# Revit family: Class-I-Fan_VBBB-CW-BHD_Carnes
name_source: partatom
category: Mechanical Equipment
revit_build: Autodesk Revit Architecture 2012 (Build: 20110309_2315(x64)
units: mm (PartAtom-declared; Revit-internal decimal feet)

## types (12) — shared parameters
04 CSI = 23 34 23
95 CSI = 15830
Angle = 270.00°
Assembly Code = D3040200
Catalog URL = http://www.carnes.com
Description = Cetrifugal Blowers
Housing = Aluminum-Carnes-Spun-Brushed
Housing Rotation CW DBD = Yes
IOM Instructions URL = http://www.carnes.com
Manufacturer = Carnes Company
Manufacturer Fax = 608-845-6470
Motor Cover = No
Product Page URL = http://www.carnes.com
URL = http://www.carnes.com
Warranty URL = http://www.carnes.com
Weather Cover = Yes
ecoScorecard Product Page = http://ecoscorecard.com
zero-valued in all types: Default Elevation

## per-type parameters (varying)
- VBBB-CW-BHD 12: 01=14.88 "; A=13 "; B=9.75 "; C=13.25 "; D=14.5 "; DX=1 "; Drip=4.88 "; Drip1=4.88 "; G=16 "; H=24.5 "; HA=9.75 "; HC=13.94 "; HE=10.56 "; HG=9.31 "; HJ=9.25 "; HN=12.94 "; J=7.44 "; KL=2 "; Model=VBBB 12; Motor Pedastal Stand=11.88 "; P=19.75 "; Radius=6.63 "; SD=1 "; SD Radius=0.5 "; SE=2.75 "; Support Plate Drip=17.63 "; Weather Cover Height=22.38 "; Weather Cover Length=17.38 "; Weather Cover Width=16 "
- VBBB-CW-BHD 13: 01=14.91 "; A=14.31 "; B=10.81 "; C=14.56 "; D=15.75 "; DX=1 "; Drip=7.4 "; Drip1=5.41 "; G=17.5 "; H=25.63 "; HA=10.75 "; HC=15.25 "; HE=11.63 "; HG=10.25 "; HJ=10.25 "; HN=14.25 "; J=8 "; KL=2 "; Model=VBBB 13; Motor Pedastal Stand=11.91 "; P=20.31 "; Radius=7.28 "; SD=1 "; SD Radius=0.5 "; SE=2.75 "; Support Plate Drip=15.75 "; Weather Cover Height=22.8 "; Weather Cover Length=17.38 "; Weather Cover Width=17.5 "
- VBBB-CW-BHD 15: 01=17.16 "; A=15.88 "; B=11.94 "; C=16.19 "; D=17.75 "; DX=1 "; Drip=6.9 "; Drip1=5.97 "; G=19 "; H=28.75 "; HA=11.94 "; HC=16.81 "; HE=12.88 "; HG=11.38 "; HJ=11.44 "; HN=15.81 "; J=9.06 "; KL=2.5 "; Model=VBBB 15; Motor Pedastal Stand=13.66 "; P=23.13 "; Radius=8.1 "; SD=1 "; SD Radius=0.5 "; SE=3.25 "; Support Plate Drip=17.75 "; Weather Cover Height=25.5 "; Weather Cover Length=19.88 "; Weather Cover Width=19 "
- VBBB-CW-BHD 16: 01=17.16 "; A=17.44 "; B=13.19 "; C=17.75 "; D=19 "; DX=1 "; Drip=6.9 "; Drip1=6.6 "; G=20.5 "; H=30.13 "; HA=13.13 "; HC=18.38 "; HE=14.13 "; HG=12.5 "; HJ=12.63 "; HN=17.38 "; J=9.69 "; KL=2.5 "; Model=VBBB 16; Motor Pedastal Stand=13.66 "; P=23.75 "; Radius=8.88 "; SD=1 "; SD Radius=0.5 "; SE=3.25 "; Support Plate Drip=19 "; Weather Cover Height=28 "; Weather Cover Length=19.88 "; Weather Cover Width=20.5 "
- VBBB-CW-BHD 18: 01=20.66 "; A=19.38 "; B=14.56 "; C=19.5 "; D=21 "; DX=1.25 "; Drip=6.4 "; Drip1=7.28 "; G=22.5 "; H=34.38 "; HA=14.5 "; HC=20.56 "; HE=15.69 "; HG=13.81 "; HJ=14 "; HN=19.31 "; J=10.88 "; KL=3 "; Model=VBBB 18; Motor Pedastal Stand=16.66 "; P=27.94 "; Radius=9.75 "; SD=1.19 "; SD Radius=0.6 "; SE=3.75 "; Support Plate Drip=21 "; Weather Cover Height=32 "; Weather Cover Length=23.25 "; Weather Cover Width=22.5 "
- VBBB-CW-BHD 20: 01=20.66 "; A=21.19 "; B=15.94 "; C=21.38 "; D=22.75 "; DX=1.25 "; Drip=6.4 "; Drip1=7.97 "; G=25 "; H=35.75 "; HA=15.81 "; HC=22.38 "; HE=17.31 "; HG=15.19 "; HJ=15.31 "; HN=21.13 "; J=11.56 "; KL=3 "; Model=VBBB 20; Motor Pedastal Stand=16.66 "; P=28.63 "; Radius=10.69 "; SD=1.44 "; SD Radius=0.72 "; SE=3.75 "; Support Plate Drip=22.75 "; Weather Cover Height=35 "; Weather Cover Length=23.38 "; Weather Cover Width=25 "
- VBBB-CW-BHD 22: 01=18.79 "; A=23.56 "; B=17.69 "; C=23.75 "; D=25.5 "; DX=1.25 "; Drip=6.4 "; Drip1=8.85 "; G=27.25 "; H=40.75 "; HA=17.69 "; HC=24.75 "; HE=19.06 "; HG=16.81 "; HJ=17.19 "; HN=23.5 "; J=12.44 "; KL=3 "; Model=VBBB 22; Motor Pedastal Stand=14.79 "; P=27.63 "; Radius=11.88 "; SD=1.44 "; SD Radius=0.72 "; SE=3.75 "; Support Plate Drip=25.5 "; Weather Cover Height=32.25 "; Weather Cover Length=20 "; Weather Cover Width=27.25 "
- VBBB-CW-BHD 24: 01=19.28 "; A=25.94 "; B=19.44 "; C=26.06 "; D=28 "; DX=1.25 "; Drip=6.4 "; Drip1=9.72 "; G=29.75 "; H=43.5 "; HA=19.5 "; HC=27.13 "; HE=21 "; HG=18.5 "; HJ=19 "; HN=25.88 "; J=13.31 "; KL=3 "; Model=VBBB 24; Motor Pedastal Stand=15.28 "; P=29 "; Radius=13.03 "; SD=1.44 "; SD Radius=0.72 "; SE=3.75 "; Support Plate Drip=28 "; Weather Cover Height=36.38 "; Weather Cover Length=21 "; Weather Cover Width=29.75 "
- VBBB-CW-BHD 27: 01=21 "; A=28.63 "; B=21.38 "; C=28.5 "; D=30.5 "; DX=1.5 "; Drip=6.4 "; Drip1=10.69 "; G=33 "; H=47.38 "; HA=21.44 "; HC=30.06 "; HE=23.19 "; HG=20.44 "; HJ=20.94 "; HN=28.56 "; J=14.25 "; KL=3.25 "; Model=VBBB 27; Motor Pedastal Stand=16.75 "; P=31.69 "; Radius=14.25 "; SD=1.44 "; SD Radius=0.72 "; SE=4 "; Support Plate Drip=30.5 "; Weather Cover Height=40.75 "; Weather Cover Length=23 "; Weather Cover Width=33 "
- VBBB-CW-BHD 30: 01=23.79 "; A=31.81 "; B=23.81 "; C=31.63 "; D=27.5 "; DX=1.5 "; Drip=6.4 "; Drip1=11.91 "; G=36.13 "; H=52.88 "; HA=23.81 "; HC=33.25 "; HE=25.75 "; HG=22.75 "; HJ=23.31 "; HN=31.75 "; J=15.5 "; KL=3 "; Model=VBBB 30; Motor Pedastal Stand=19.79 "; P=35.69 "; Radius=15.82 "; SD=1.94 "; SD Radius=0.97 "; SE=3.75 "; Support Plate Drip=27.5 "; Weather Cover Height=38 "; Weather Cover Length=29.94 "; Weather Cover Width=36.13 "
- VBBB-CW-BHD 33: 01=24.78 "; A=35.13 "; B=26.06 "; C=34.75 "; D=30 "; DX=1.5 "; Drip=6.4 "; Drip1=13.03 "; G=38.88 "; H=56.13 "; HA=26.25 "; HC=36.56 "; HE=28.38 "; HG=25 "; HJ=25.75 "; HN=35.06 "; J=16.63 "; KL=3 "; Model=VBBB 33; Motor Pedastal Stand=20.78 "; P=37.81 "; Radius=17.38 "; SD=1.94 "; SD Radius=0.97 "; SE=3.75 "; Support Plate Drip=30 "; Weather Cover Height=40.5 "; Weather Cover Length=30.94 "; Weather Cover Width=38.88 "
- VBBB-CW-BHD 36: 01=36.12 "; A=38.75 "; B=28.88 "; C=38.5 "; D=33.5 "; DX=1.5 "; Drip=6.5 "; Drip1=14.44 "; G=43.75 "; H=64.56 "; HA=29 "; HC=40.13 "; HE=31.5 "; HG=27.75 "; HJ=28.5 "; HN=39.63 "; J=18 "; KL=4 "; Model=VBBB 36; Motor Pedastal Stand=31.12 "; P=50.56 "; Radius=19.25 "; SD=1.94 "; SD Radius=0.97 "; SE=4.75 "; Support Plate Drip=33.5 "; Weather Cover Height=46.25 "; Weather Cover Length=38.19 "; Weather Cover Width=43.75 "

## geometry (parser evidence)
native form markers: Blend x2, Sweep x41
no freeform markers — native parametric forms only
